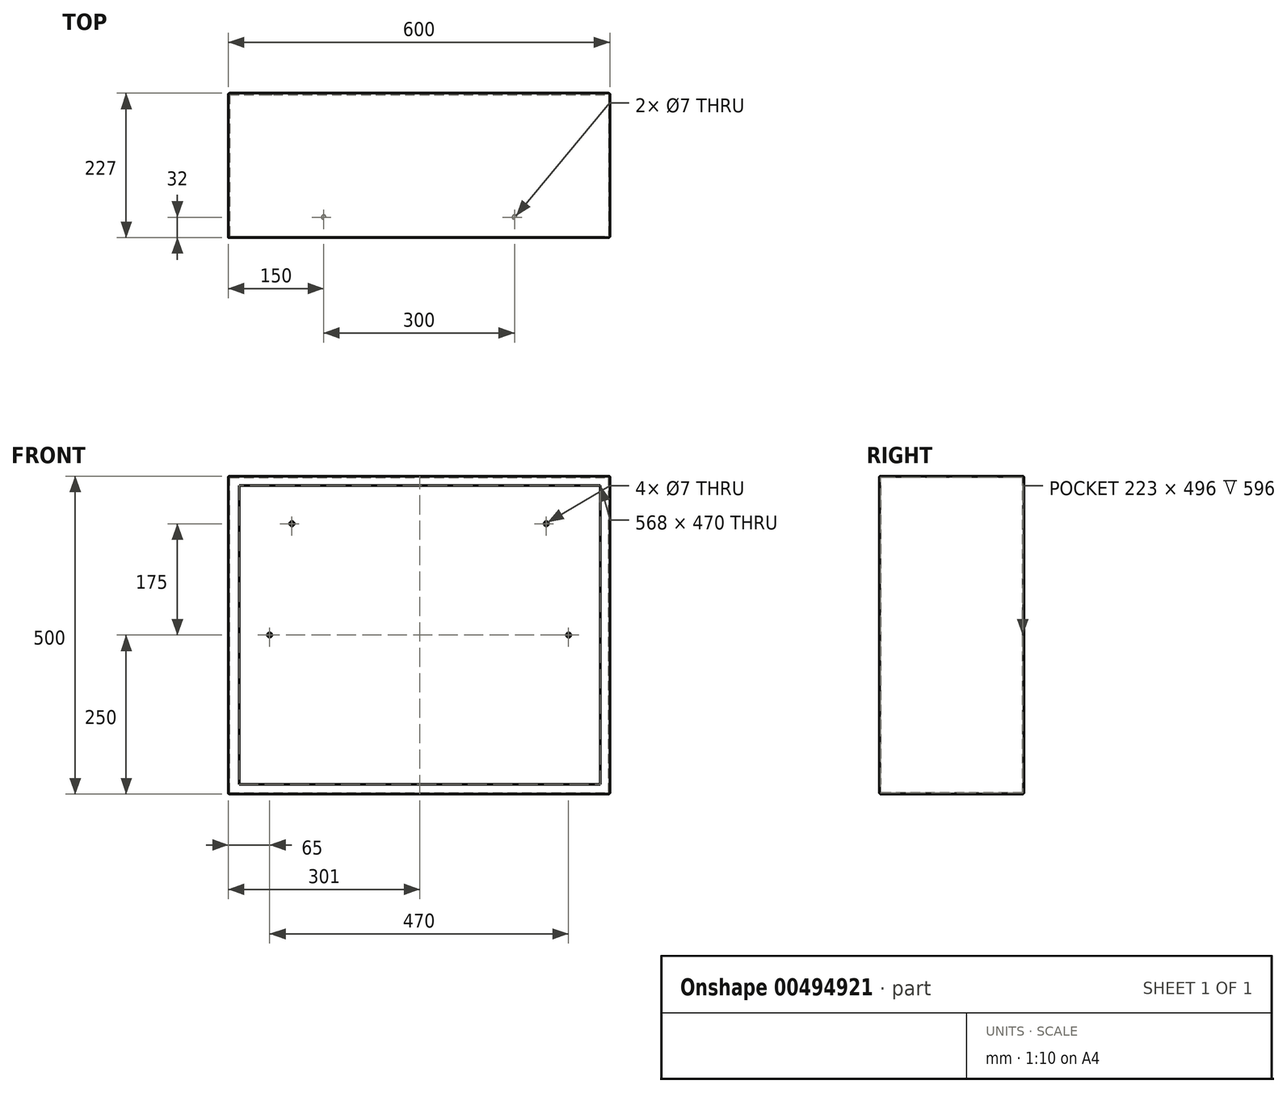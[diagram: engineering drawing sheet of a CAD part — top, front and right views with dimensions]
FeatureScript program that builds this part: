
annotation { "Feature Type Name" : "Feature", "Feature Type Description" : "" }
export const myFeature = defineFeature(function(context is Context, id is Id, definition is map)
    precondition{}
    {
        {
            var Q0;
            Q0=qCreatedBy(makeId("Front.planeOp"),FACE);
            var sketch = newSketch(context, id + "F0", { "sketchPlane" : qUnion([Q0])});
            skLineSegment(sketch, "E0.bottom", {"start": v(-300, -300) * mm, "end": v(300, -300) * mm});
            skLineSegment(sketch, "E0.top", {"start": v(-300, 200) * mm, "end": v(300, 200) * mm});
            skLineSegment(sketch, "E0.left", {"start": v(-300, -300) * mm, "end": v(-300, 200) * mm});
            skLineSegment(sketch, "E0.right", {"start": v(300, -300) * mm, "end": v(300, 200) * mm});
            skSolve(sketch);
        }
        {
            var Q0;
            Q0=qSketchRegion(id+"F0",true);
            extrude(context, id + "F1", {"entities" : qUnion([Q0]), "oppositeDirection" : true, "depth" : 225 * mm});
        }
        {
            var Q0;
            Q0=makeQuery(id+"F1.opExtrude","CAP_FACE",FACE,{"disambiguationData":[OSD([sQuery(id+"F0.wireOp",EDGE,"E0.bottom"),sQuery(id+"F0.wireOp",EDGE,"E0.top"),sQuery(id+"F0.wireOp",EDGE,"E0.left"),sQuery(id+"F0.wireOp",EDGE,"E0.right")])],"isStart":true});
            shell(context, id + "F2", {"entities" : qUnion([Q0]), "thickness" : 2 * mm});
        }
        {
            var Q0;
            Q0=qCreatedBy(makeId("Front.planeOp"),FACE);
            var sketch = newSketch(context, id + "F3", { "sketchPlane" : qUnion([Q0])});
            skLineSegment(sketch, "E1.top", {"start": v(300, -300) * mm, "end": v(300, -300) * mm});
            skLineSegment(sketch, "E1.right", {"start": v(300, 200) * mm, "end": v(300, -300) * mm});
            skLineSegment(sketch, "E2.bottom", {"start": v(-283, 185) * mm, "end": v(285, 185) * mm});
            skLineSegment(sketch, "E2.top", {"start": v(-283, -285) * mm, "end": v(285, -285) * mm});
            skLineSegment(sketch, "E2.left", {"start": v(-283, 185) * mm, "end": v(-283, -285) * mm});
            skLineSegment(sketch, "E2.right", {"start": v(285, 185) * mm, "end": v(285, -285) * mm});
            skLineSegment(sketch, "E3", {"start": v(300, 200) * mm, "end": v(-300, 200) * mm});
            skLineSegment(sketch, "E4", {"start": v(-300, 200) * mm, "end": v(-300, -300) * mm});
            skLineSegment(sketch, "E5", {"start": v(300, -300) * mm, "end": v(-300, -300) * mm});
            skSolve(sketch);
        }
        {
            var Q0;
            Q0=qSketchRegion(id+"F3",true);
            extrude(context, id + "F4", {"entities" : qUnion([Q0]), "operationType" : NewBodyOperationType.ADD, "depth" : 2 * mm});
        }
        {
            var Q0;
            Q0=makeQuery(id+"F2.opShell","OFFSET_FACE",FACE,{"disambiguationData":[OSD([sQuery(id+"F0.wireOp",EDGE,"E0.bottom"),sQuery(id+"F0.wireOp",EDGE,"E0.top"),sQuery(id+"F0.wireOp",EDGE,"E0.left"),sQuery(id+"F0.wireOp",EDGE,"E0.right")])]});
            var sketch = newSketch(context, id + "F5", { "sketchPlane" : qUnion([Q0])});
            skPoint(sketch, "E6", {"position": v(-200, 125) * mm});
            skPoint(sketch, "E7", {"position": v(200, 125) * mm});
            skPoint(sketch, "E8", {"position": v(-235, -50) * mm});
            skPoint(sketch, "E9", {"position": v(235, -50) * mm});
            skSolve(sketch);
        }
        {
            var Q0;
            Q0=sQuery(id+"F5.wireOp",VERTEX,"E6");
            var Q1;
            Q1=sQuery(id+"F5.wireOp",VERTEX,"E7");
            var Q2;
            Q2=sQuery(id+"F5.wireOp",VERTEX,"E9");
            var Q3;
            Q3=sQuery(id+"F5.wireOp",VERTEX,"E8");
            var Q4;
            Q4=makeQuery(id+"F1.opExtrude","SWEPT_BODY",BODY,{"disambiguationData":[OSD([sQuery(id+"F0.wireOp",EDGE,"E0.bottom"),sQuery(id+"F0.wireOp",EDGE,"E0.top"),sQuery(id+"F0.wireOp",EDGE,"E0.left"),sQuery(id+"F0.wireOp",EDGE,"E0.right")])]});
            hole(context, id + "F6", {"style" : HoleStyle.SIMPLE, "endStyle" : HoleEndStyle.THROUGH, "holeDiameter" : 7 * mm, "isTappedThrough" : true, "tappedDepth" : 15 * mm, "tapClearance" : 3, "locations" : qUnion([Q0, Q1, Q2, Q3]), "scope" : qUnion([Q4])});
        }
        {
            var Q0;
            Q0=makeQuery(id+"F4.boolean.opBoolean","MERGE",FACE,{"derivedFrom":[makeQuery(id+"F1.opExtrude","SWEPT_FACE",FACE,{"disambiguationData":[OSD([sQuery(id+"F0.wireOp",EDGE,"E0.bottom")])]}),makeQuery(id+"F4.opExtrude","SWEPT_FACE",FACE,{"disambiguationData":[OSD([sQuery(id+"F3.wireOp",EDGE,"E1.top")])]})]});
            var sketch = newSketch(context, id + "F7", { "sketchPlane" : qUnion([Q0])});
            skPoint(sketch, "E10", {"position": v(-150, -30) * mm});
            skPoint(sketch, "E11", {"position": v(150, -30) * mm});
            skSolve(sketch);
        }
        {
            var Q0;
            Q0=sQuery(id+"F7.wireOp",VERTEX,"E11");
            var Q1;
            Q1=sQuery(id+"F7.wireOp",VERTEX,"E10");
            var Q2;
            Q2=makeQuery(id+"F1.opExtrude","SWEPT_BODY",BODY,{"disambiguationData":[OSD([sQuery(id+"F0.wireOp",EDGE,"E0.bottom"),sQuery(id+"F0.wireOp",EDGE,"E0.top"),sQuery(id+"F0.wireOp",EDGE,"E0.left"),sQuery(id+"F0.wireOp",EDGE,"E0.right")])]});
            hole(context, id + "F8", {"style" : HoleStyle.SIMPLE, "endStyle" : HoleEndStyle.BLIND, "holeDiameter" : 7 * mm, "holeDepth" : 18 * mm, "isTappedThrough" : true, "tappedDepth" : 15 * mm, "tapClearance" : 3, "locations" : qUnion([Q0, Q1]), "scope" : qUnion([Q2])});
        }
        {
            var Q0;
            Q0=makeQuery(id+"F4.opExtrude","CAP_EDGE",EDGE,{"disambiguationData":[OSD([sQuery(id+"F3.wireOp",EDGE,"E3")])],"isStart":false});
            var Q1;
            Q1=makeQuery(id+"F4.boolean.opBoolean","MERGE",EDGE,{"derivedFrom":[makeQuery(id+"F1.opExtrude","SWEPT_EDGE",EDGE,{"disambiguationData":[OSD([sQuery(id+"F0.wireOp",EDGE,"E0.top"),sQuery(id+"F0.wireOp",EDGE,"E0.right")])]}),makeQuery(id+"F4.opExtrude","SWEPT_EDGE",EDGE,{"disambiguationData":[OSD([sQuery(id+"F3.wireOp",EDGE,"E1.right"),sQuery(id+"F3.wireOp",EDGE,"E3")])]})]});
            var Q2;
            Q2=makeQuery(id+"F1.opExtrude","CAP_EDGE",EDGE,{"disambiguationData":[OSD([sQuery(id+"F0.wireOp",EDGE,"E0.top")])],"isStart":false});
            var Q3;
            Q3=makeQuery(id+"F4.boolean.opBoolean","MERGE",EDGE,{"derivedFrom":[makeQuery(id+"F1.opExtrude","SWEPT_EDGE",EDGE,{"disambiguationData":[OSD([sQuery(id+"F0.wireOp",EDGE,"E0.top"),sQuery(id+"F0.wireOp",EDGE,"E0.left")])]}),makeQuery(id+"F4.opExtrude","SWEPT_EDGE",EDGE,{"disambiguationData":[OSD([sQuery(id+"F3.wireOp",EDGE,"E3"),sQuery(id+"F3.wireOp",EDGE,"E4")])]})]});
            var Q4;
            Q4=makeQuery(id+"F4.opExtrude","CAP_EDGE",EDGE,{"disambiguationData":[OSD([sQuery(id+"F3.wireOp",EDGE,"E5")])],"isStart":false});
            var Q5;
            Q5=makeQuery(id+"F1.opExtrude","CAP_EDGE",EDGE,{"disambiguationData":[OSD([sQuery(id+"F0.wireOp",EDGE,"E0.bottom")])],"isStart":false});
            var Q6;
            Q6=makeQuery(id+"F4.boolean.opBoolean","MERGE",EDGE,{"derivedFrom":[makeQuery(id+"F1.opExtrude","SWEPT_EDGE",EDGE,{"disambiguationData":[OSD([sQuery(id+"F0.wireOp",EDGE,"E0.bottom"),sQuery(id+"F0.wireOp",EDGE,"E0.left")])]}),makeQuery(id+"F4.opExtrude","SWEPT_EDGE",EDGE,{"disambiguationData":[OSD([sQuery(id+"F3.wireOp",EDGE,"E4"),sQuery(id+"F3.wireOp",EDGE,"E5")])]})]});
            var Q7;
            Q7=makeQuery(id+"F4.boolean.opBoolean","MERGE",EDGE,{"derivedFrom":[makeQuery(id+"F1.opExtrude","SWEPT_EDGE",EDGE,{"disambiguationData":[OSD([sQuery(id+"F0.wireOp",EDGE,"E0.bottom"),sQuery(id+"F0.wireOp",EDGE,"E0.right")])]}),makeQuery(id+"F4.opExtrude","SWEPT_EDGE",EDGE,{"disambiguationData":[OSD([sQuery(id+"F3.wireOp",EDGE,"E1.right"),sQuery(id+"F3.wireOp",EDGE,"E5")])]})]});
            var Q8;
            Q8=makeQuery(id+"F1.opExtrude","CAP_EDGE",EDGE,{"disambiguationData":[OSD([sQuery(id+"F0.wireOp",EDGE,"E0.right")])],"isStart":false});
            var Q9;
            Q9=makeQuery(id+"F4.opExtrude","CAP_EDGE",EDGE,{"disambiguationData":[OSD([sQuery(id+"F3.wireOp",EDGE,"E1.right")])],"isStart":false});
            var Q10;
            Q10=makeQuery(id+"F1.opExtrude","CAP_EDGE",EDGE,{"disambiguationData":[OSD([sQuery(id+"F0.wireOp",EDGE,"E0.left")])],"isStart":false});
            fillet(context, id + "F9", {"entities" : qUnion([Q0, Q1, Q2, Q3, Q4, Q5, Q6, Q7, Q8, Q9, Q10]), "radius" : 2 * mm, "tangentPropagation" : true, "allowEdgeOverflow" : false});
        }
    });
